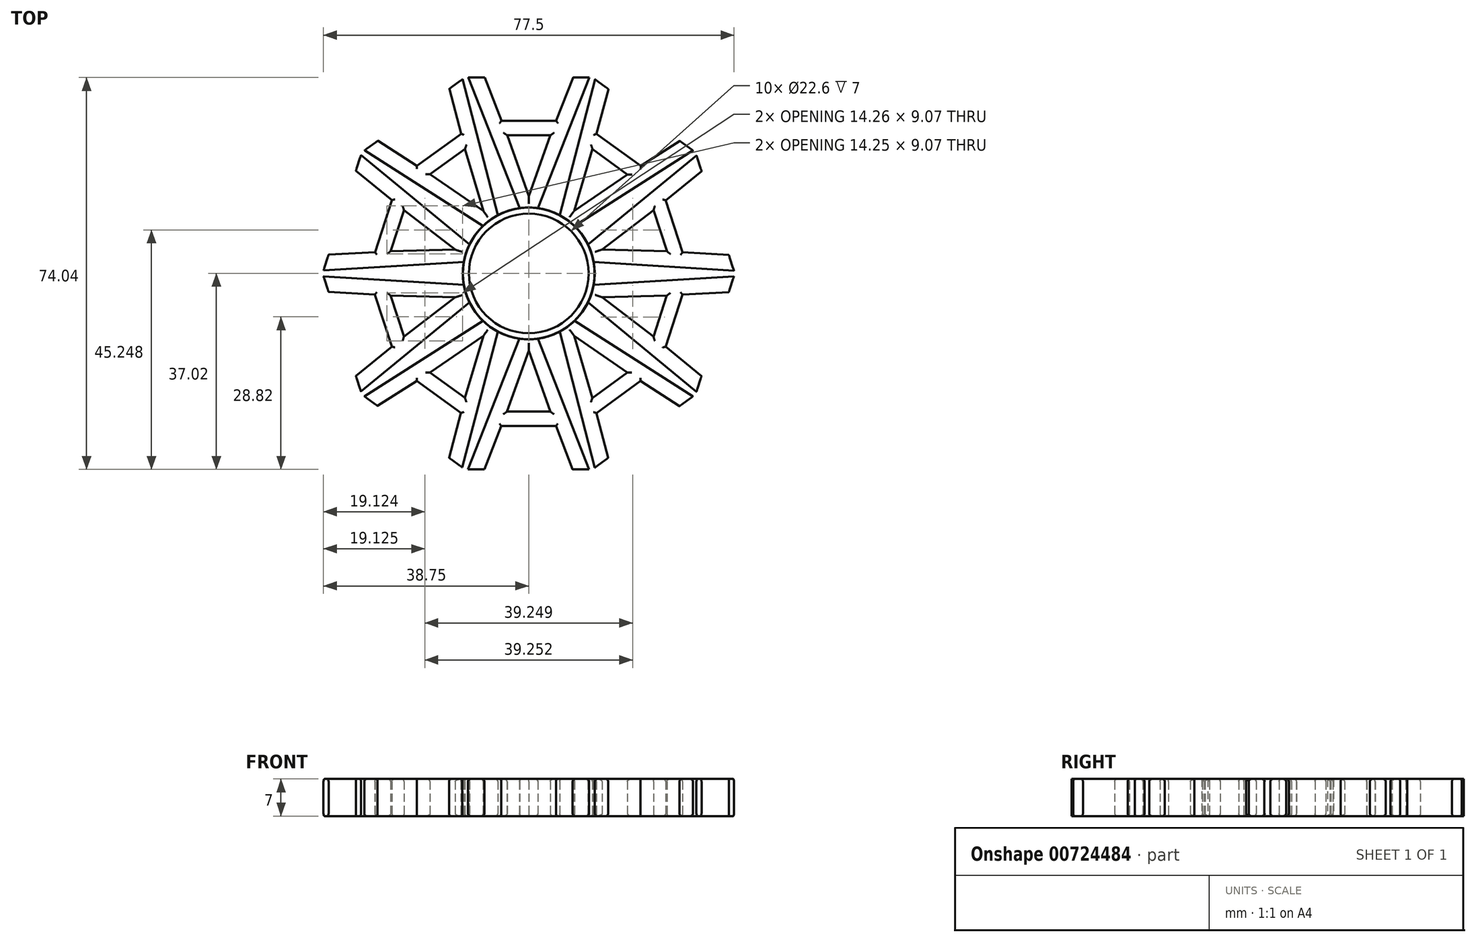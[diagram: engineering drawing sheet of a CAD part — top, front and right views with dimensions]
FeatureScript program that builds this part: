
annotation { "Feature Type Name" : "Feature", "Feature Type Description" : "" }
export const myFeature = defineFeature(function(context is Context, id is Id, definition is map)
    precondition{}
    {
        {
            var Q0;
            Q0=qCreatedBy(makeId("Top.planeOp"),FACE);
            var sketch = newSketch(context, id + "F0", { "sketchPlane" : qUnion([Q0])});
            skCircle(sketch, "E0", {"center": v(0, 0) * mm, "radius": 11.3 * mm});
            skLineSegment(sketch, "E1", {"start": v(11.46, 37.02) * mm, "end": v(1.26, 11.13) * mm});
            skLineSegment(sketch, "E2", {"start": v(-1.26, 11.13) * mm, "end": v(-11.4, 37.02) * mm});
            skLineSegment(sketch, "E3", {"start": v(-11.4, 37.02) * mm, "end": v(-8.3, 37.02) * mm});
            skLineSegment(sketch, "E4", {"start": v(-8.3, 37.02) * mm, "end": v(-5.15, 28.85) * mm});
            skLineSegment(sketch, "E5", {"start": v(-5.15, 28.85) * mm, "end": v(5.18, 28.85) * mm});
            skLineSegment(sketch, "E6", {"start": v(5.18, 28.85) * mm, "end": v(8.37, 37.02) * mm});
            skLineSegment(sketch, "E7", {"start": v(8.37, 37.02) * mm, "end": v(11.46, 37.02) * mm});
            skLineSegment(sketch, "E8", {"start": v(4.1, 26.1) * mm, "end": v(-4.07, 26.1) * mm});
            skLineSegment(sketch, "E9", {"start": v(-4.07, 26.1) * mm, "end": v(0, 14.59) * mm});
            skLineSegment(sketch, "E10", {"start": v(0, 14.59) * mm, "end": v(4.1, 26.1) * mm});
            skCircle(sketch, "E11", {"center": v(0, 0) * mm, "radius": 12.44 * mm});
            skSolve(sketch);
        }
        {
            var Q0;
            Q0 = qSketchRegion(id + "F0", true);
            extrude(context, id + "F1", {"entities" : qUnion([Q0]), "depth" : 7 * mm, "offsetDistance" : 25 * mm});
        }
        {
            var Q0;
            Q0=makeQuery(id+"F1.opExtrude","CAP_EDGE",EDGE,{"disambiguationData":[OSD([sQuery(id+"F0.wireOp",EDGE,"d5789443-62f4-4617-8a18-e69ce41c4897.9.8")])],"isStart":false});
            var Q1;
            Q1=makeQuery(id+"F1.opExtrude","CAP_EDGE",EDGE,{"disambiguationData":[OSD([sQuery(id+"F0.wireOp",EDGE,"E2")])],"isStart":false});
            var Q2;
            Q2=makeQuery(id+"F1.opExtrude","CAP_EDGE",EDGE,{"disambiguationData":[OSD([sQuery(id+"F0.wireOp",EDGE,"E1")])],"isStart":false});
            var Q3;
            Q3=makeQuery(id+"F1.opExtrude","CAP_EDGE",EDGE,{"disambiguationData":[OSD([sQuery(id+"F0.wireOp",EDGE,"E1")])],"isStart":true});
            var Q4;
            Q4=makeQuery(id+"F1.opExtrude","CAP_EDGE",EDGE,{"disambiguationData":[OSD([sQuery(id+"F0.wireOp",EDGE,"E2")])],"isStart":true});
            var Q5;
            Q5=makeQuery(id+"F1.opExtrude","CAP_EDGE",EDGE,{"disambiguationData":[OSD([sQuery(id+"F0.wireOp",EDGE,"E6")])],"isStart":false});
            var Q6;
            Q6=makeQuery(id+"F1.opExtrude","CAP_EDGE",EDGE,{"disambiguationData":[OSD([sQuery(id+"F0.wireOp",EDGE,"E10")])],"isStart":false});
            var Q7;
            Q7=makeQuery(id+"F1.opExtrude","CAP_EDGE",EDGE,{"disambiguationData":[OSD([sQuery(id+"F0.wireOp",EDGE,"E9")])],"isStart":false});
            var Q8;
            Q8=makeQuery(id+"F1.opExtrude","CAP_EDGE",EDGE,{"disambiguationData":[OSD([sQuery(id+"F0.wireOp",EDGE,"E4")])],"isStart":false});
            var Q9;
            Q9=makeQuery(id+"F1.opExtrude","CAP_EDGE",EDGE,{"disambiguationData":[OSD([sQuery(id+"F0.wireOp",EDGE,"E8")])],"isStart":false});
            var Q10;
            Q10=makeQuery(id+"F1.opExtrude","CAP_EDGE",EDGE,{"disambiguationData":[OSD([sQuery(id+"F0.wireOp",EDGE,"E5")])],"isStart":false});
            var Q11;
            Q11=makeQuery(id+"F1.opExtrude","CAP_EDGE",EDGE,{"disambiguationData":[OSD([sQuery(id+"F0.wireOp",EDGE,"E5")])],"isStart":true});
            var Q12;
            Q12=makeQuery(id+"F1.opExtrude","CAP_EDGE",EDGE,{"disambiguationData":[OSD([sQuery(id+"F0.wireOp",EDGE,"E8")])],"isStart":true});
            var Q13;
            Q13=makeQuery(id+"F1.opExtrude","CAP_EDGE",EDGE,{"disambiguationData":[OSD([sQuery(id+"F0.wireOp",EDGE,"E10")])],"isStart":true});
            var Q14;
            Q14=makeQuery(id+"F1.opExtrude","CAP_EDGE",EDGE,{"disambiguationData":[OSD([sQuery(id+"F0.wireOp",EDGE,"E9")])],"isStart":true});
            var Q15;
            Q15=makeQuery(id+"F1.opExtrude","CAP_EDGE",EDGE,{"disambiguationData":[OSD([sQuery(id+"F0.wireOp",EDGE,"E4")])],"isStart":true});
            var Q16;
            Q16=makeQuery(id+"F1.opExtrude","CAP_EDGE",EDGE,{"disambiguationData":[OSD([sQuery(id+"F0.wireOp",EDGE,"E6")])],"isStart":true});
            fillet(context, id + "F2", {"entities" : qUnion([Q0, Q1, Q2, Q3, Q4, Q5, Q6, Q7, Q8, Q9, Q10, Q11, Q12, Q13, Q14, Q15, Q16]), "radius" : 0.48 * mm, "tangentPropagation" : true, "allowEdgeOverflow" : false});
        }
        {
            var Q0;
            Q0=makeQuery(id+"F1.opExtrude","SWEPT_BODY",BODY,{"disambiguationData":[OSD([sQuery(id+"F0.wireOp",EDGE,"E0"),sQuery(id+"F0.wireOp",EDGE,"E1"),sQuery(id+"F0.wireOp",EDGE,"E2"),sQuery(id+"F0.wireOp",EDGE,"E3"),sQuery(id+"F0.wireOp",EDGE,"E4"),sQuery(id+"F0.wireOp",EDGE,"E5"),sQuery(id+"F0.wireOp",EDGE,"E6"),sQuery(id+"F0.wireOp",EDGE,"E7"),sQuery(id+"F0.wireOp",EDGE,"E8"),sQuery(id+"F0.wireOp",EDGE,"E9"),sQuery(id+"F0.wireOp",EDGE,"E10"),sQuery(id+"F0.wireOp",EDGE,"E11")])]});
            var Q1;
            Q1=makeQuery(id+"F1.opExtrude","SWEPT_FACE",FACE,{"disambiguationData":[OSD([sQuery(id+"F0.wireOp",EDGE,"E11")])]});
            circularPattern(context, id + "F3", {"entities" : qUnion([Q0]), "axis" : qUnion([Q1]), "angle" : 360 * degree, "instanceCount" : 10, "equalSpace" : true});
        }
    });
